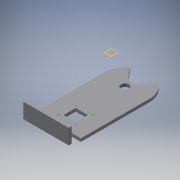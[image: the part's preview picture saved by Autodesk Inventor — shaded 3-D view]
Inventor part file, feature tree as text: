
AUTODESK INVENTOR PART (.ipt)
format: ipt  version: 2018.3 (Build 223284000, 284)  size: 135,168 bytes
history: native  units: mm
features: other x2, extrude x2, sketch x2
ambient origin geometry x8: Origin, YZ Plane, XZ Plane, XY Plane, X Axis, Y Axis, Z Axis, Center Point
bodies: Body1 (feature_tree)
feature tree (6):
  other  "РабПлоскость1"
  extrude  "Выдавливание1"  Depth=10.0mm TaperAngle=0.0deg
  extrude  "Выдавливание2"  Depth=50.0mm TaperAngle=0.0deg
  sketch  "Эскиз1"
  other  "Твердое тело2"
  sketch  "Эскиз2"
